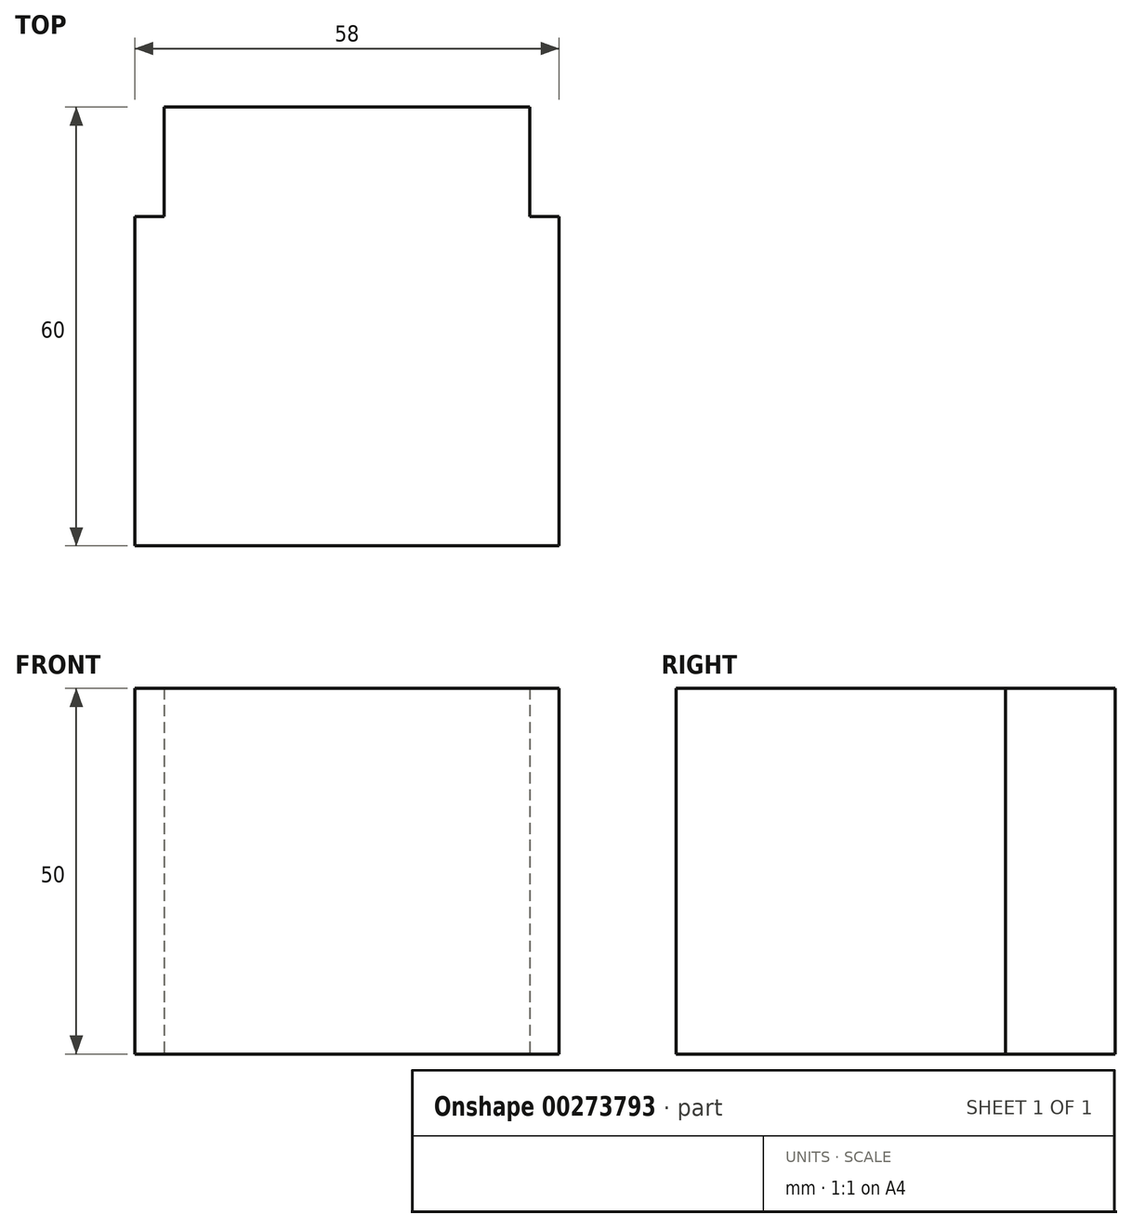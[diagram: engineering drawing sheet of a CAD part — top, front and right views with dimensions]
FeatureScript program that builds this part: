
annotation { "Feature Type Name" : "Feature", "Feature Type Description" : "" }
export const myFeature = defineFeature(function(context is Context, id is Id, definition is map)
    precondition{}
    {
        {
            var Q0;
            Q0=qCreatedBy(makeId("Front.planeOp"),FACE);
            var sketch = newSketch(context, id + "F0", { "sketchPlane" : qUnion([Q0])});
            skLineSegment(sketch, "E0.bottom", {"start": v(-27.36, 11.17) * mm, "end": v(30.64, 11.17) * mm});
            skLineSegment(sketch, "E0.top", {"start": v(-27.36, -38.83) * mm, "end": v(30.64, -38.83) * mm});
            skLineSegment(sketch, "E0.left", {"start": v(-27.36, 11.17) * mm, "end": v(-27.36, -38.83) * mm});
            skLineSegment(sketch, "E0.right", {"start": v(30.64, 11.17) * mm, "end": v(30.64, -38.83) * mm});
            skSolve(sketch);
        }
        {
            var Q0;
            Q0=makeQuery(id+"F0.imprint","IMPRINT",FACE,{"disambiguationData":[TD([[makeQuery(id+"F0.imprint","IMPRINT",EDGE,{"derivedFrom":sQuery(id+"F0.wireOp",EDGE,"E0.bottom")}),-1.0]])]});
            extrude(context, id + "F1", {"entities" : qUnion([Q0]), "depth" : 60 * mm});
        }
        {
            var Q0;
            Q0=makeQuery(id+"F1.opExtrude","SWEPT_FACE",FACE,{"disambiguationData":[OSD([sQuery(id+"F0.wireOp",EDGE,"E0.top")])]});
            var sketch = newSketch(context, id + "F2", { "sketchPlane" : qUnion([Q0])});
            skLineSegment(sketch, "E1.bottom", {"start": v(-23.36, 15) * mm, "end": v(-27.36, 15) * mm});
            skLineSegment(sketch, "E1.top", {"start": v(-23.36, 0) * mm, "end": v(-27.36, 0) * mm});
            skLineSegment(sketch, "E1.left", {"start": v(-23.36, 15) * mm, "end": v(-23.36, 0) * mm});
            skLineSegment(sketch, "E1.right", {"start": v(-27.36, 15) * mm, "end": v(-27.36, 0) * mm});
            skLineSegment(sketch, "E2.bottom", {"start": v(26.64, 15) * mm, "end": v(30.64, 15) * mm});
            skLineSegment(sketch, "E2.top", {"start": v(26.64, 0) * mm, "end": v(30.64, 0) * mm});
            skLineSegment(sketch, "E2.left", {"start": v(26.64, 15) * mm, "end": v(26.64, 0) * mm});
            skLineSegment(sketch, "E2.right", {"start": v(30.64, 15) * mm, "end": v(30.64, 0) * mm});
            skSolve(sketch);
        }
        {
            var Q0;
            Q0=makeQuery(id+"F2.imprint","IMPRINT",FACE,{"disambiguationData":[TD([[makeQuery(id+"F2.imprint","IMPRINT",EDGE,{"derivedFrom":sQuery(id+"F2.wireOp",EDGE,"E1.bottom")}),1.0]])]});
            var Q1;
            Q1=makeQuery(id+"F2.imprint","IMPRINT",FACE,{"disambiguationData":[TD([[makeQuery(id+"F2.imprint","IMPRINT",EDGE,{"derivedFrom":sQuery(id+"F2.wireOp",EDGE,"E2.bottom")}),-1.0]])]});
            extrude(context, id + "F3", {"entities" : qUnion([Q0, Q1]), "operationType" : NewBodyOperationType.REMOVE, "oppositeDirection" : true, "depth" : 50 * mm});
        }
    });
